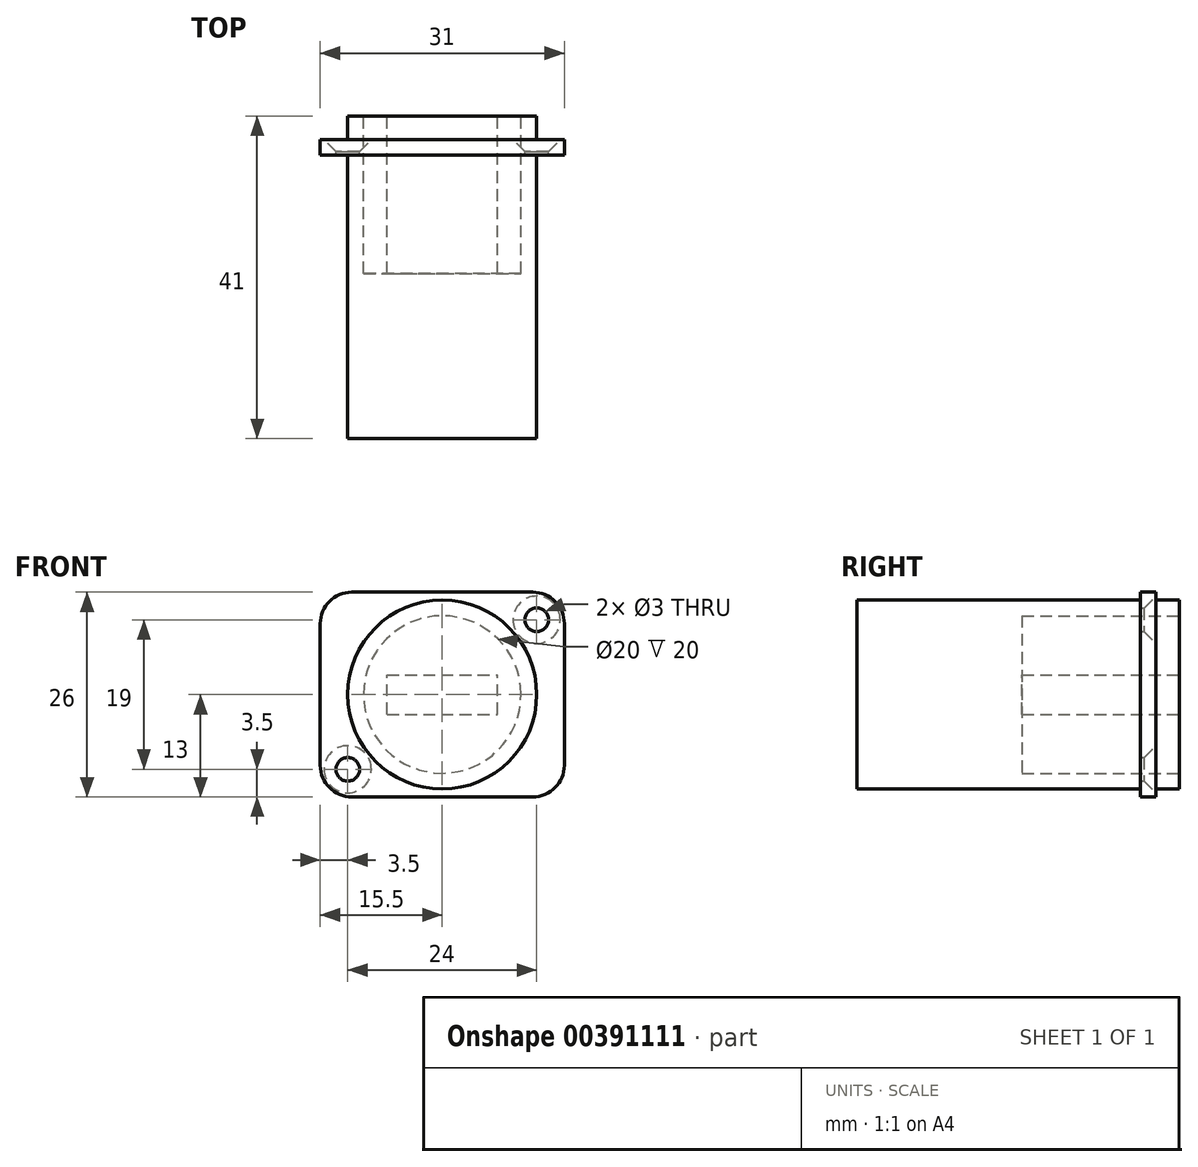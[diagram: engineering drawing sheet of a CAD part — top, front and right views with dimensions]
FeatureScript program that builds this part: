
annotation { "Feature Type Name" : "Feature", "Feature Type Description" : "" }
export const myFeature = defineFeature(function(context is Context, id is Id, definition is map)
    precondition{}
    {
        {
            var Q0;
            Q0=qCreatedBy(makeId("Front.planeOp"),FACE);
            var sketch = newSketch(context, id + "F0", { "sketchPlane" : qUnion([Q0])});
            skLineSegment(sketch, "E0.bottom", {"start": v(4, 0) * mm, "end": v(27, 0) * mm});
            skLineSegment(sketch, "E0.top", {"start": v(4, 26) * mm, "end": v(27, 26) * mm});
            skLineSegment(sketch, "E0.left", {"start": v(0, 4) * mm, "end": v(0, 22) * mm});
            skLineSegment(sketch, "E0.right", {"start": v(31, 4) * mm, "end": v(31, 22) * mm});
            skPoint(sketch, "E1.visualSharp", {"position": v(31, 26) * mm});
            skArc(sketch, "E1.filletArc", {"start": v(31, 22) * mm, "mid": v(29.83, 24.83) * mm, "end": v(27, 26) * mm});
            skPoint(sketch, "E2.visualSharp", {"position": v(0, 26) * mm});
            skArc(sketch, "E2.filletArc", {"start": v(4, 26) * mm, "mid": v(1.17, 24.83) * mm, "end": v(0, 22) * mm});
            skPoint(sketch, "E3.visualSharp", {"position": v(0, 0) * mm});
            skArc(sketch, "E3.filletArc", {"start": v(0, 4) * mm, "mid": v(1.17, 1.17) * mm, "end": v(4, 0) * mm});
            skPoint(sketch, "E4.visualSharp", {"position": v(31, 0) * mm});
            skArc(sketch, "E4.filletArc", {"start": v(27, 0) * mm, "mid": v(29.83, 1.17) * mm, "end": v(31, 4) * mm});
            skLineSegment(sketch, "E5.bottom", {"start": v(3.5, 22.5) * mm, "end": v(27.5, 22.5) * mm, "construction": true});
            skLineSegment(sketch, "E5.top", {"start": v(3.5, 3.5) * mm, "end": v(27.5, 3.5) * mm, "construction": true});
            skLineSegment(sketch, "E5.left", {"start": v(3.5, 22.5) * mm, "end": v(3.5, 3.5) * mm, "construction": true});
            skLineSegment(sketch, "E5.right", {"start": v(27.5, 22.5) * mm, "end": v(27.5, 3.5) * mm, "construction": true});
            skPoint(sketch, "E6.startSnap1", {"position": v(15.5, 22.5) * mm});
            skLineSegment(sketch, "E7", {"start": v(15.5, 26) * mm, "end": v(15.5, 0) * mm, "construction": true});
            skLineSegment(sketch, "E8", {"start": v(0, 13) * mm, "end": v(31, 13) * mm, "construction": true});
            skPoint(sketch, "E9", {"position": v(3.5, 13) * mm});
            skSolve(sketch);
        }
        {
            var Q0;
            Q0=qSketchRegion(id+"F0",true);
            extrude(context, id + "F1", {"entities" : qUnion([Q0]), "depth" : 2 * mm});
        }
        {
            var Q0;
            Q0=sQuery(id+"F0.wireOp",VERTEX,"E5.right.start");
            var Q1;
            Q1=sQuery(id+"F0.wireOp",VERTEX,"E5.top.start");
            var Q2;
            Q2=makeQuery(id+"F1.opExtrude","SWEPT_BODY",BODY,{"disambiguationData":[OSD([sQuery(id+"F0.wireOp",EDGE,"E0.bottom"),sQuery(id+"F0.wireOp",EDGE,"E0.top"),sQuery(id+"F0.wireOp",EDGE,"E0.left"),sQuery(id+"F0.wireOp",EDGE,"E0.right"),sQuery(id+"F0.wireOp",EDGE,"E1.filletArc"),sQuery(id+"F0.wireOp",EDGE,"E2.filletArc"),sQuery(id+"F0.wireOp",EDGE,"E3.filletArc"),sQuery(id+"F0.wireOp",EDGE,"E4.filletArc")])]});
            hole(context, id + "F2", {"style" : HoleStyle.C_SINK, "endStyle" : HoleEndStyle.THROUGH, "oppositeDirection" : true, "holeDiameter" : 3 * mm, "cSinkDiameter" : 6 * mm, "cSinkAngle" : 90 * degree, "isTappedThrough" : true, "tappedDepth" : 12 * mm, "tapClearance" : 3, "locations" : qUnion([Q0, Q1]), "scope" : qUnion([Q2])});
        }
        {
            var Q0;
            Q0=makeQuery(id+"F1.opExtrude","CAP_FACE",FACE,{"disambiguationData":[OSD([sQuery(id+"F0.wireOp",EDGE,"E0.bottom"),sQuery(id+"F0.wireOp",EDGE,"E0.top"),sQuery(id+"F0.wireOp",EDGE,"E0.left"),sQuery(id+"F0.wireOp",EDGE,"E0.right"),sQuery(id+"F0.wireOp",EDGE,"E1.filletArc"),sQuery(id+"F0.wireOp",EDGE,"E2.filletArc"),sQuery(id+"F0.wireOp",EDGE,"E3.filletArc"),sQuery(id+"F0.wireOp",EDGE,"E4.filletArc")])],"isStart":true});
            var sketch = newSketch(context, id + "F3", { "sketchPlane" : qUnion([Q0])});
            skCircle(sketch, "E10", {"center": v(-15.5, 13) * mm, "radius": 12 * mm});
            skSolve(sketch);
        }
        {
            var Q0;
            Q0=qSketchRegion(id+"F3",true);
            extrude(context, id + "F4", {"entities" : qUnion([Q0]), "operationType" : NewBodyOperationType.ADD, "depth" : 3 * mm});
        }
        {
            var Q0;
            Q0=qSketchRegion(id+"F3",true);
            extrude(context, id + "F5", {"entities" : qUnion([Q0]), "operationType" : NewBodyOperationType.ADD, "oppositeDirection" : true, "depth" : 38 * mm});
        }
        {
            var Q0;
            Q0=makeQuery(id+"F4.opExtrude","CAP_FACE",FACE,{"disambiguationData":[OSD([sQuery(id+"F3.wireOp",EDGE,"E10")])],"isStart":false});
            var sketch = newSketch(context, id + "F6", { "sketchPlane" : qUnion([Q0])});
            skCircle(sketch, "E11", {"center": v(-15.5, 13) * mm, "radius": 10 * mm});
            skLineSegment(sketch, "E12.bottom", {"start": v(-8.5, 10.5) * mm, "end": v(-22.5, 10.5) * mm});
            skLineSegment(sketch, "E12.top", {"start": v(-8.5, 15.5) * mm, "end": v(-22.5, 15.5) * mm});
            skLineSegment(sketch, "E12.left", {"start": v(-8.5, 10.5) * mm, "end": v(-8.5, 15.5) * mm});
            skLineSegment(sketch, "E12.right", {"start": v(-22.5, 10.5) * mm, "end": v(-22.5, 15.5) * mm});
            skSolve(sketch);
        }
        {
            var Q0;
            Q0=qSketchRegion(id+"F6",true);
            extrude(context, id + "F7", {"entities" : qUnion([Q0]), "operationType" : NewBodyOperationType.REMOVE, "oppositeDirection" : true, "depth" : 20 * mm});
        }
    });
